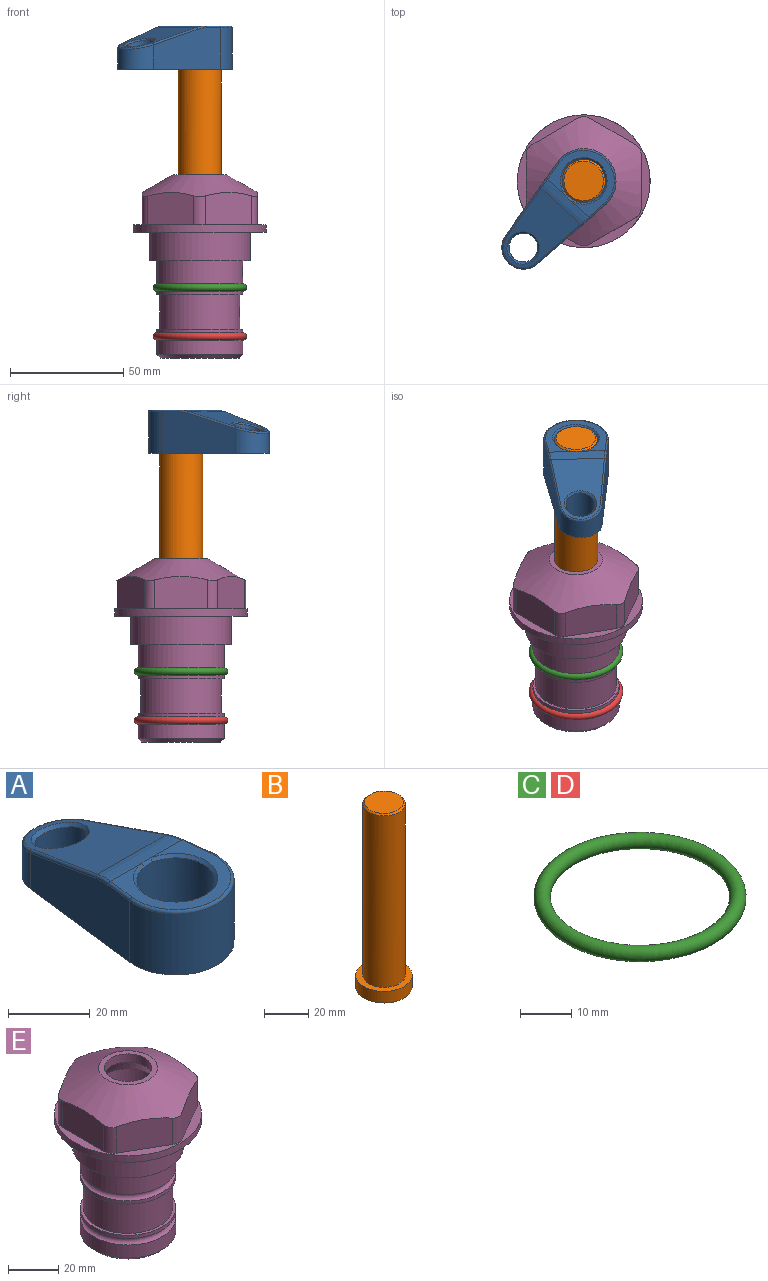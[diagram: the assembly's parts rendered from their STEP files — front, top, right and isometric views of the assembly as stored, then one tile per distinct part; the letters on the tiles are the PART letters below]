
ASSEMBLY  parts=5 mates=4
PART A: 31 faces, bbox 31.7x65.5x19.8 mm
  f0: plane 39.12x18.26mm, normal (0.99,0.12,0), area 612.2mm2, adj f1,f4,f7,f11,f13,f15
  f1: cylinder r=9.53mm len=18.91mm, axis (0,0,-1), area 296.1mm2, adj f0,f2,f7,f17
  f2: plane 39.12x18.26mm, normal (-0.99,0.12,0), area 612.2mm2, adj f1,f4,f7,f12,f14,f16
  f3: cylinder r=6.35mm len=12.7mm, axis (0,0,-1), area 362.4mm2, adj f7,f18
  f4: cylinder r=14.29mm len=28.58mm, axis (0,0,-1), area 882.2mm2, adj f0,f2,f7,f10
  f5: cylinder r=9.53mm len=19.05mm, axis (0,0,-1), area 1092.6mm2, adj f7,f19,f20
  f6: plane 26.99x23.69mm, normal (0,0,1), area 216.2mm2, adj f9,f10,f11,f12,f19
  f7: plane 63.5x28.58mm, normal (0,0,-1), area 661.8mm2, adj f0,f1,f2,f3,f4,f5,f22,f23
  f8: plane 33.52x23.6mm, normal (0,0.26,0.97), area 486mm2, adj f9,f15,f16,f17,f18
  f9: cylinder r=19.05mm len=24.72mm, axis (1,0,0), area 120.4mm2, adj f6,f8,f13,f14,f20
  f10: torus R=13.49mm, axis (0,0,1), area 59mm2, adj f4,f6,f11,f12
  f11: cylinder r=0.79mm len=8.67mm, axis (0.12,-0.99,0), area 10.8mm2, adj f0,f6,f10,f13
  f12: cylinder r=0.79mm len=8.67mm, axis (0.12,0.99,0), area 10.8mm2, adj f2,f6,f10,f14
  f13: bspline ~4.95x1.42mm, area 6.1mm2, adj f0,f9,f11,f15
  f14: bspline ~4.95x1.42mm, area 6.1mm2, adj f2,f9,f12,f16
  f15: cylinder r=0.79mm len=25.95mm, axis (0.12,-0.96,0.26), area 32.9mm2, adj f0,f8,f13,f17
  f16: cylinder r=0.79mm len=25.95mm, axis (0.12,0.96,-0.26), area 32.9mm2, adj f2,f8,f14,f17
  f17: bspline ~18.91x8.38mm, area 30mm2, adj f1,f8,f15,f16
  f18: bspline ~14.29x14.29mm, area 48.3mm2, adj f3,f8
  f19: cone r=9.53mm half-angle=45deg, axis (0,0,1), area 66.5mm2, adj f5,f6,f20
  f20: bspline ~3.22x0.96mm, area 3.5mm2, adj f5,f9,f19
  f21: plane 2.75x2.72mm, normal (0,0,-1), area 2.9mm2, adj f23,f25,f28
  f22: plane 23.05x15.88mm, normal (-0.99,-0.12,0), area 323.6mm2, adj f7,f25,f26,f27,f28,f29
  f23: plane 23.05x15.88mm, normal (0.99,-0.12,0), area 323.6mm2, adj f7,f21,f25,f27,f28,f30
  f24: cylinder r=9.53mm len=10.69mm, axis (0,0,-1), area 114.7mm2, adj f7,f27,f29,f30
  f25: cylinder r=12.7mm len=20.59mm, axis (0,0,-1), area 381.1mm2, adj f7,f21,f22,f23,f26,f28
  f26: plane 2.75x2.72mm, normal (0,0,-1), area 2.9mm2, adj f22,f25,f28
  f27: plane 19.72x18.37mm, normal (0,-0.26,-0.97), area 291.8mm2, adj f22,f23,f24,f28,f29,f30
  f28: cylinder r=15.88mm len=19.92mm, axis (1,0,0), area 54.8mm2, adj f21,f22,f23,f25,f26,f27
  f29: cylinder r=1.59mm len=11mm, axis (0,0,-1), area 34.7mm2, adj f7,f22,f24,f27
  f30: cylinder r=1.59mm len=11mm, axis (0,0,-1), area 34.7mm2, adj f7,f23,f24,f27
PART B: 6 faces, bbox 25.4x25.4x101.6 mm
  f0: plane 17.46x17.46mm, normal (0,0,1), area 239.5mm2, adj f5
  f1: plane 25.4x25.4mm, normal (0,0,-1), area 506.7mm2, adj f2
  f2: cylinder r=12.7mm len=25.4mm, axis (0,0,1), area 506.7mm2, adj f1,f3
  f3: plane 25.4x25.4mm, normal (0,0,1), area 221.7mm2, adj f2,f4
  f4: cylinder r=9.53mm len=94.46mm, axis (0,0,1), area 5653mm2, adj f3,f5
  f5: cone r=8.73mm half-angle=45deg, axis (0,0,-1), area 64.4mm2, adj f0,f4
PART C: 1 faces, bbox 44.7x44.7x3.2 mm
  f0: torus R=19.05mm, axis (0,0,1), area 1193.9mm2
PART D: same geometry as C
PART E: 36 faces, bbox 58.7x58.7x81 mm
  f0: cylinder r=17.78mm len=35.56mm, axis (0,0,1), area 1670.8mm2, adj f23,f24,f31
  f1: cylinder r=19.05mm len=38.1mm, axis (0,0,1), area 1191.9mm2, adj f26,f27,f30
  f2: plane 58.66x58.66mm, normal (0,0,-1), area 1150.6mm2, adj f3,f28
  f3: cylinder r=29.33mm len=58.66mm, axis (0,0,-1), area 585.1mm2, adj f2,f4
  f4: plane 58.66x58.66mm, normal (0,0,1), area 475.9mm2, adj f3,f5,f6,f7,f8,f9,f10,f11
  f5: plane 20.32x14.34mm, normal (-0.5,0.87,0), area 324.4mm2, adj f4,f15,f16,f17
  f6: plane 20.32x14.34mm, normal (0.5,0.87,0), area 324.4mm2, adj f4,f14,f15,f17
  f7: plane 23.48x14.34mm, normal (1,0,0), area 324.4mm2, adj f4,f13,f14,f17
  f8: plane 20.32x14.34mm, normal (0.5,-0.87,0), area 324.4mm2, adj f4,f12,f13,f17
  f9: plane 20.32x14.34mm, normal (-0.5,-0.87,0), area 324.4mm2, adj f4,f11,f12,f17
  f10: plane 23.48x14.34mm, normal (-1,0,0), area 324.4mm2, adj f4,f11,f16,f17
  f11: cylinder r=5.08mm len=12.85mm, axis (0,0,-1), area 67.2mm2, adj f4,f9,f10,f17
  f12: cylinder r=5.08mm len=12.85mm, axis (0,0,-1), area 67.2mm2, adj f4,f8,f9,f17
  f13: cylinder r=5.08mm len=12.85mm, axis (0,0,-1), area 67.2mm2, adj f4,f7,f8,f17
  f14: cylinder r=5.08mm len=12.85mm, axis (0,0,-1), area 67.2mm2, adj f4,f6,f7,f17
  f15: cylinder r=5.08mm len=12.85mm, axis (0,0,-1), area 67.2mm2, adj f4,f5,f6,f17
  f16: cylinder r=5.08mm len=12.85mm, axis (0,0,-1), area 67.2mm2, adj f4,f5,f10,f17
  f17: cone r=11.73mm half-angle=60deg, axis (0,0,-1), area 2071.8mm2, adj f5,f6,f7,f8,f9,f10,f11,f12
  f18: plane 23.46x23.46mm, normal (0,0,1), area 147.4mm2, adj f17,f35
  f19: plane 34.93x34.93mm, normal (0,0,-1), area 958mm2, adj f29
  f20: cylinder r=19.05mm len=38.1mm, axis (0,0,1), area 760.1mm2, adj f21,f29
  f21: torus R=19.05mm, axis (0,0,1), area 565.3mm2, adj f20,f22
  f22: cylinder r=19.05mm len=38.1mm, axis (0,0,1), area 190mm2, adj f21,f23
  f23: plane 38.1x38.1mm, normal (0,0,1), area 146.9mm2, adj f0,f22
  f24: plane 38.1x38.1mm, normal (0,0,-1), area 146.9mm2, adj f0,f25
  f25: cylinder r=19.05mm len=38.1mm, axis (0,0,1), area 190mm2, adj f24,f26
  f26: torus R=19.05mm, axis (0,0,1), area 565.3mm2, adj f1,f25
  f27: plane 44.45x44.45mm, normal (0,0,-1), area 411.7mm2, adj f1,f28
  f28: cylinder r=22.23mm len=44.45mm, axis (0,0,1), area 1773.5mm2, adj f2,f27
  f29: cone r=19.05mm half-angle=45deg, axis (0,0,1), area 257.5mm2, adj f19,f20
  f30: cylinder r=3.17mm len=6.75mm, axis (-1,0,0), area 128mm2, adj f1,f33
  f31: cylinder r=3.17mm len=6.35mm, axis (-1,0,0), area 102.5mm2, adj f0,f33
  f32: plane 25.4x25.4mm, normal (0,0,1), area 506.7mm2, adj f33
  f33: cylinder r=12.7mm len=66.42mm, axis (0,0,-1), area 5236.2mm2, adj f30,f31,f32,f34
  f34: cone r=9.53mm half-angle=30deg, axis (0,0,-1), area 443.4mm2, adj f33,f35
  f35: cylinder r=9.53mm len=19.05mm, axis (0,0,-1), area 240.9mm2, adj f18,f34
PLACE A rot(axis=(0,0,1),137.9deg) t=(0,0,27.55)mm
PLACE B rot(axis=(0,0,1),137.9deg) t=(0,0,27.55)mm
PLACE C at identity
PLACE D t=(0,0,-21.59)mm
PLACE E at identity fixed
MATE cylindrical B.f2 <-> E.f0  axis (0,0,-1) through (0,0,-10.55)mm
MATE fastened D.f0 <-> E.f0  axis (0,0,1) through (0,0,-46.1)mm
MATE fastened B.f2 <-> A.f4  axis (0,0,1) through (0,0,91.05)mm
MATE fastened C.f0 <-> E.f0  axis (0,0,1) through (0,0,-24.51)mm
